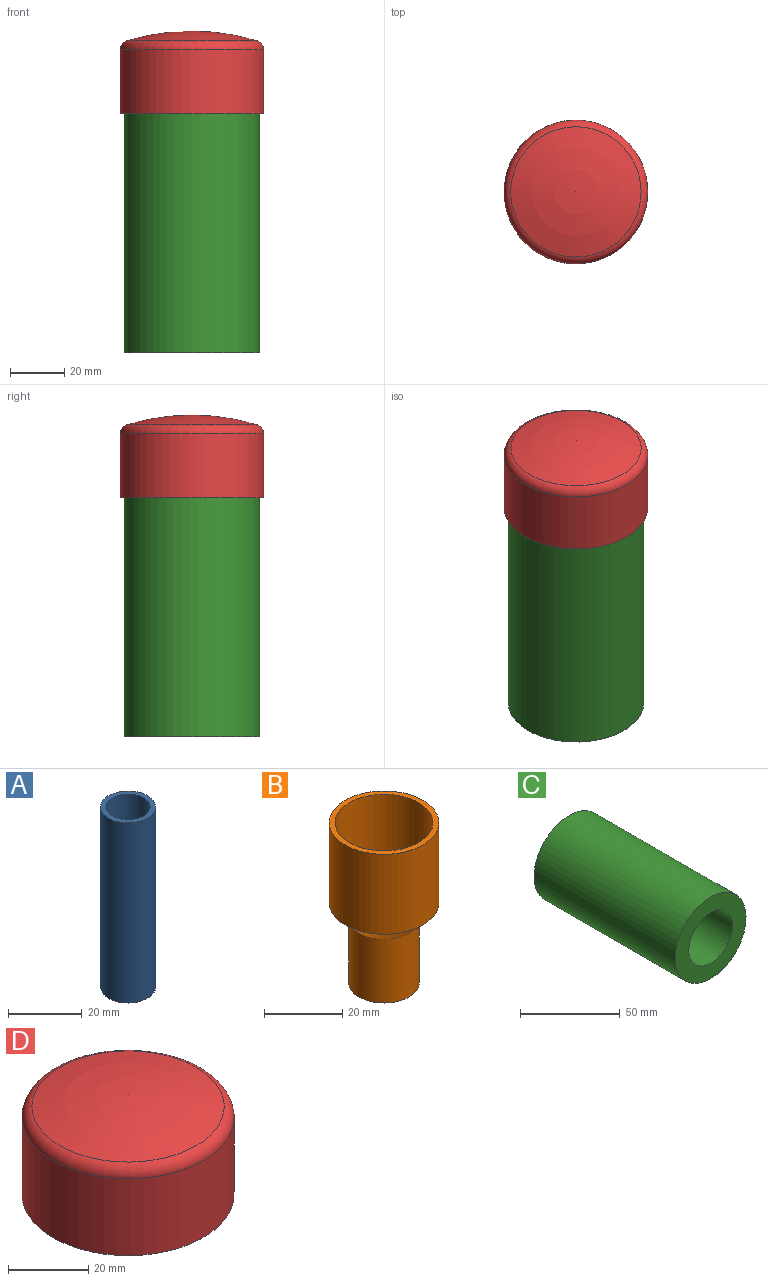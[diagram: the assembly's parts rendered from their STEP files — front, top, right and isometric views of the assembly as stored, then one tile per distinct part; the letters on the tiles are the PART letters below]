
ASSEMBLY  parts=4 mates=3
PART A: 4 faces, bbox 15x15x60 mm
  f0: cylinder r=7.5mm len=60mm, axis (0,0,-1), area 2827.4mm2, adj f1,f2
  f1: plane 15x15mm, normal (0,0,1), area 63.6mm2, adj f0,f3
  f2: plane 15x15mm, normal (0,0,-1), area 63.6mm2, adj f0,f3
  f3: cylinder r=6mm len=60mm, axis (0,0,-1), area 2261.9mm2, adj f1,f2
PART B: 8 faces, bbox 28x28x50 mm
  f0: cylinder r=9mm len=20mm, axis (0,0,-1), area 1131mm2, adj f1,f4
  f1: plane 18x18mm, normal (0,0,-1), area 77.8mm2, adj f0,f5
  f2: cylinder r=14mm len=28mm, axis (0,0,-1), area 2199.1mm2, adj f3,f4
  f3: plane 28x28mm, normal (0,0,1), area 124.9mm2, adj f2,f6
  f4: cone r=14mm half-angle=45deg, axis (0,0,1), area 510.9mm2, adj f0,f2
  f5: cylinder r=7.5mm len=20.62mm, axis (0,0,-1), area 971.8mm2, adj f1,f7
  f6: cylinder r=12.5mm len=25mm, axis (0,0,-1), area 1914.7mm2, adj f3,f7
  f7: cone r=12.94mm half-angle=45deg, axis (0,0,1), area 444.3mm2, adj f5,f6
PART C: 4 faces, bbox 50x100x50 mm
  f0: cylinder r=15.5mm len=100mm, axis (0,1,0), area 9738.9mm2, adj f2,f3
  f1: cylinder r=25mm len=100mm, axis (0,1,0), area 15708mm2, adj f2,f3
  f2: plane 50x50mm, normal (0,-1,0), area 1208.7mm2, adj f0,f1
  f3: plane 50x50mm, normal (0,1,0), area 1208.7mm2, adj f0,f1
PART D: 7 faces, bbox 57.4x57.4x30.5 mm
  f0: cylinder r=25mm len=50mm, axis (0,0,1), area 3697.3mm2, adj f1,f6
  f1: plane 53x53mm, normal (0,0,-1), area 242.7mm2, adj f0,f2
  f2: cylinder r=26.5mm len=53mm, axis (0,0,1), area 3919.1mm2, adj f1,f3
  f3: torus R=23mm, axis (0,0,1), area 716.9mm2, adj f2,f4
  f4: sphere r=81.63mm, area 1855.2mm2, adj f3
  f5: sphere r=80.13mm, area 1787.7mm2, adj f6
  f6: torus R=23mm, axis (0,0,1), area 391.7mm2, adj f0,f5
PLACE A at identity fixed
PLACE B t=(0,0,49.69)mm
PLACE C rot(axis=(-1,0,0),90deg) t=(0,0,0)mm
PLACE D t=(0,0,88.23)mm
MATE fastened D.f0 <-> C.f1  axis (0,0,1) through (0,0,100)mm
MATE fastened B.f0 <-> A.f0  axis (0,0,-1) through (0,0,60)mm
MATE fastened C.f1 <-> A.f0  axis (0,0,-1) through (0,0,0)mm
